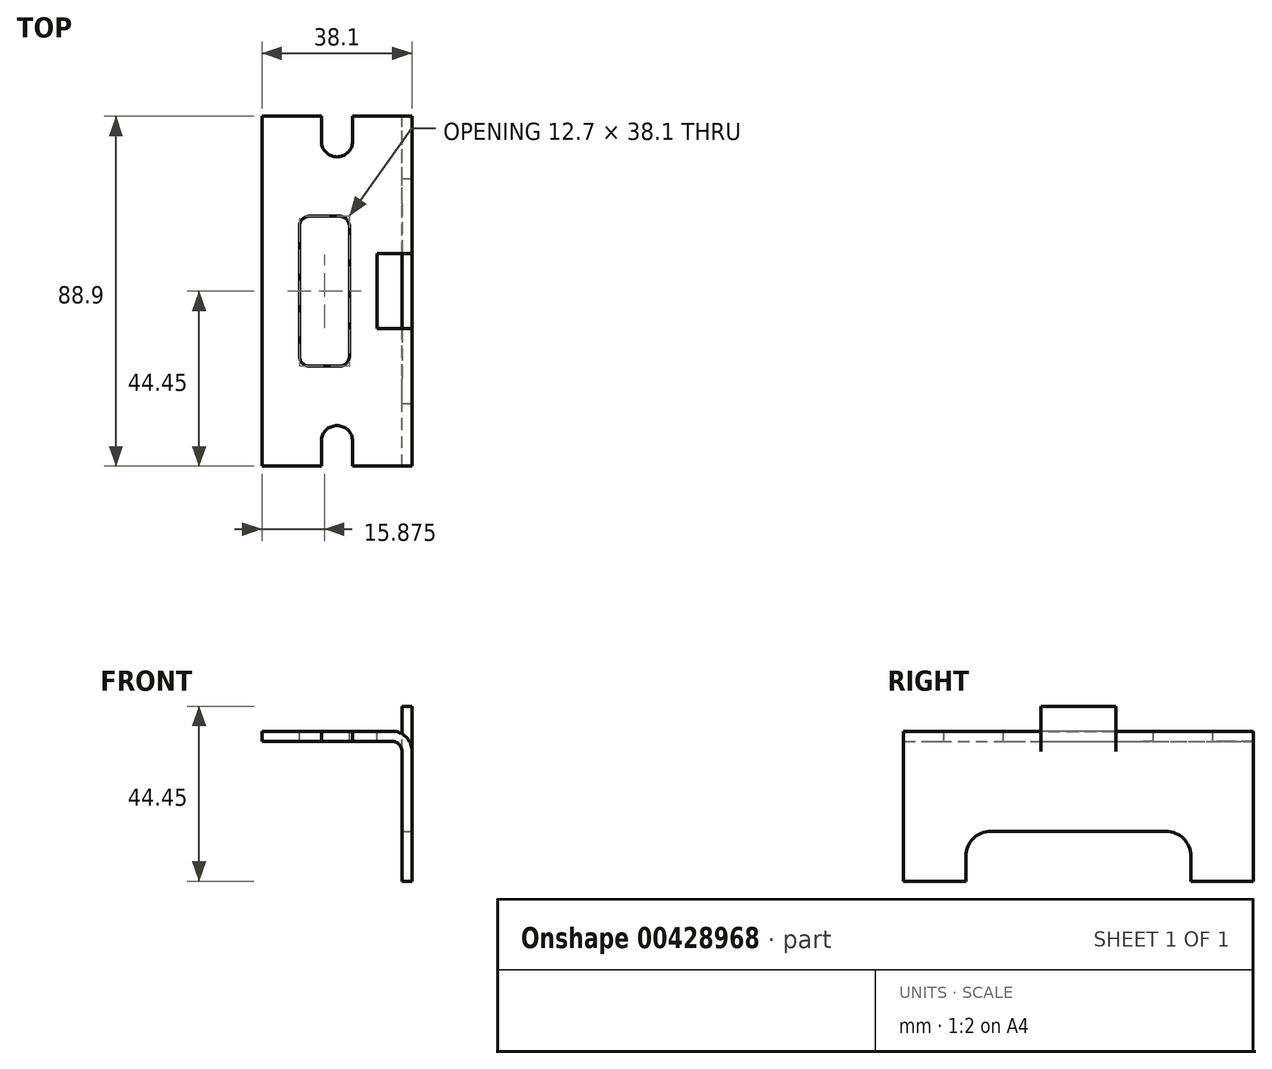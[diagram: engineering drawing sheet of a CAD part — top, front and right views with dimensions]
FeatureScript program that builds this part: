
annotation { "Feature Type Name" : "Feature", "Feature Type Description" : "" }
export const myFeature = defineFeature(function(context is Context, id is Id, definition is map)
    precondition{}
    {
        {
            var Q0;
            Q0=qCreatedBy(makeId("Front.planeOp"),FACE);
            var sketch = newSketch(context, id + "F0", { "sketchPlane" : qUnion([Q0])});
            skLineSegment(sketch, "E0", {"start": v(-5.08, 0) * mm, "end": v(-38.1, 0) * mm});
            skLineSegment(sketch, "E1", {"start": v(0, -38.1) * mm, "end": v(-2.54, -38.1) * mm});
            skLineSegment(sketch, "E2", {"start": v(-2.54, -38.1) * mm, "end": v(-2.54, -5.08) * mm});
            skLineSegment(sketch, "E3", {"start": v(-5.08, -2.54) * mm, "end": v(-38.1, -2.54) * mm});
            skLineSegment(sketch, "E4", {"start": v(-38.1, -2.54) * mm, "end": v(-38.1, 0) * mm});
            skPoint(sketch, "E5.visualSharp", {"position": v(-2.54, -2.54) * mm});
            skArc(sketch, "E5.filletArc", {"start": v(-2.54, -5.08) * mm, "mid": v(-3.28, -3.28) * mm, "end": v(-5.08, -2.54) * mm});
            skLineSegment(sketch, "E6", {"start": v(0, -38.1) * mm, "end": v(0, -3.75) * mm});
            skArc(sketch, "E7.0", {"start": v(0, -5.08) * mm, "mid": v(-1.49, -1.49) * mm, "end": v(-5.08, 0) * mm});
            skPoint(sketch, "E8.orphan", {"position": v(0, 0) * mm});
            skSolve(sketch);
        }
        {
            var Q0;
            Q0 = qSketchRegion(id + "F0", true);
            extrude(context, id + "F1", {"entities" : qUnion([Q0]), "depth" : 88.9 * mm});
        }
        {
            var Q0;
            Q0=makeQuery(id+"F1.opExtrude","SWEPT_FACE",FACE,{"disambiguationData":[OSD([sQuery(id+"F0.wireOp",EDGE,"E0")])]});
            var sketch = newSketch(context, id + "F2", { "sketchPlane" : qUnion([Q0])});
            skLineSegment(sketch, "E9.bottom", {"start": v(-2.54, -34.93) * mm, "end": v(-8.9, -34.93) * mm});
            skLineSegment(sketch, "E9.top", {"start": v(-2.54, -53.98) * mm, "end": v(-8.9, -53.98) * mm});
            skLineSegment(sketch, "E9.left", {"start": v(-2.54, -34.93) * mm, "end": v(-2.54, -53.98) * mm});
            skLineSegment(sketch, "E9.right", {"start": v(-8.9, -34.93) * mm, "end": v(-8.9, -53.98) * mm});
            skPoint(sketch, "E10.bottom.start.orphan", {"position": v(-21.59, -88.9) * mm});
            skPoint(sketch, "E10.top.end.orphan", {"position": v(-5.72, -53.98) * mm});
            skSolve(sketch);
        }
        {
            var Q0;
            Q0=makeQuery(id+"F2.imprint","IMPRINT",FACE,{"disambiguationData":[TD([[makeQuery(id+"F2.imprint","IMPRINT",EDGE,{"derivedFrom":sQuery(id+"F2.wireOp",EDGE,"E9.bottom")}),1.0]])]});
            extrude(context, id + "F3", {"entities" : qUnion([Q0]), "operationType" : NewBodyOperationType.REMOVE, "oppositeDirection" : true, "depth" : 25.4 * mm});
        }
        {
            var Q0;
            Q0=makeQuery(id+"F1.opExtrude","SWEPT_FACE",FACE,{"disambiguationData":[OSD([sQuery(id+"F0.wireOp",EDGE,"E0")])]});
            var sketch = newSketch(context, id + "F4", { "sketchPlane" : qUnion([Q0])});
            skLineSegment(sketch, "E11.bottom", {"start": v(-2.54, -34.93) * mm, "end": v(0, -34.93) * mm});
            skLineSegment(sketch, "E11.top", {"start": v(-2.54, -53.98) * mm, "end": v(0, -53.98) * mm});
            skLineSegment(sketch, "E11.left", {"start": v(-2.54, -34.93) * mm, "end": v(-2.54, -53.98) * mm});
            skLineSegment(sketch, "E11.right", {"start": v(0, -34.93) * mm, "end": v(0, -53.98) * mm});
            skSolve(sketch);
        }
        {
            var Q0;
            Q0 = qSketchRegion(id + "F4", true);
            extrude(context, id + "F5", {"entities" : qUnion([Q0]), "operationType" : NewBodyOperationType.ADD, "depth" : 6.35 * mm, "hasSecondDirection" : true, "secondDirectionOppositeDirection" : true, "secondDirectionDepth" : 6.35 * mm});
        }
        {
            var Q0;
            {var subQ0=sQuery(id+"F2.wireOp",EDGE,"E9.right");Q0=makeQuery(id+"F2.imprint","IMPRINT",FACE,{"disambiguationData":[TD([[makeQuery(id+"F2.imprint","IMPRINT",EDGE,{"derivedFrom":subQ0}),-1.0]])]});}
            var sketch = newSketch(context, id + "F6", { "sketchPlane" : qUnion([Q0])});
            skArc(sketch, "E12", {"start": v(-23.02, -6.35) * mm, "mid": v(-19.05, -10.32) * mm, "end": v(-15.08, -6.35) * mm});
            skArc(sketch, "E13", {"start": v(-15.08, -82.55) * mm, "mid": v(-19.05, -78.58) * mm, "end": v(-23.02, -82.55) * mm});
            skLineSegment(sketch, "E14", {"start": v(-23.02, -6.35) * mm, "end": v(-23.02, 0) * mm});
            skLineSegment(sketch, "E15", {"start": v(-15.08, -6.35) * mm, "end": v(-15.08, 0) * mm});
            skPoint(sketch, "E16.start.orphan", {"position": v(-19.05, 0) * mm});
            skLineSegment(sketch, "E17", {"start": v(-23.02, 0) * mm, "end": v(-15.08, 0) * mm});
            skLineSegment(sketch, "E18", {"start": v(-15.08, -82.55) * mm, "end": v(-15.08, -89) * mm});
            skLineSegment(sketch, "E19", {"start": v(-23.02, -82.55) * mm, "end": v(-23.02, -89) * mm});
            skLineSegment(sketch, "E20", {"start": v(-23.02, -89) * mm, "end": v(-15.08, -89) * mm});
            skSolve(sketch);
        }
        {
            var Q0;
            Q0 = qSketchRegion(id + "F6", true);
            extrude(context, id + "F7", {"entities" : qUnion([Q0]), "operationType" : NewBodyOperationType.REMOVE, "oppositeDirection" : true, "depth" : 25.4 * mm});
        }
        {
            var Q0;
            {var subQ0=sQuery(id+"F2.wireOp",EDGE,"E9.right");Q0=makeQuery(id+"F2.imprint","IMPRINT",FACE,{"disambiguationData":[TD([[makeQuery(id+"F2.imprint","IMPRINT",EDGE,{"derivedFrom":subQ0}),-1.0]])]});}
            var sketch = newSketch(context, id + "F8", { "sketchPlane" : qUnion([Q0])});
            skLineSegment(sketch, "E21.bottom", {"start": v(-26.04, -25.4) * mm, "end": v(-18.42, -25.4) * mm});
            skLineSegment(sketch, "E21.top", {"start": v(-26.03, -63.5) * mm, "end": v(-18.41, -63.5) * mm});
            skLineSegment(sketch, "E21.left", {"start": v(-28.58, -27.94) * mm, "end": v(-28.57, -60.96) * mm});
            skLineSegment(sketch, "E21.right", {"start": v(-15.88, -27.94) * mm, "end": v(-15.87, -60.96) * mm});
            skPoint(sketch, "E22.visualSharp", {"position": v(-28.58, -25.4) * mm});
            skArc(sketch, "E22.filletArc", {"start": v(-26.04, -25.4) * mm, "mid": v(-27.83, -26.14) * mm, "end": v(-28.58, -27.94) * mm});
            skPoint(sketch, "E23.visualSharp", {"position": v(-15.88, -25.4) * mm});
            skArc(sketch, "E23.filletArc", {"start": v(-15.88, -27.94) * mm, "mid": v(-16.62, -26.14) * mm, "end": v(-18.42, -25.4) * mm});
            skPoint(sketch, "E24.visualSharp", {"position": v(-28.57, -63.5) * mm});
            skArc(sketch, "E24.filletArc", {"start": v(-28.57, -60.96) * mm, "mid": v(-27.83, -62.76) * mm, "end": v(-26.03, -63.5) * mm});
            skPoint(sketch, "E25.visualSharp", {"position": v(-15.87, -63.5) * mm});
            skArc(sketch, "E25.filletArc", {"start": v(-18.41, -63.5) * mm, "mid": v(-16.62, -62.76) * mm, "end": v(-15.88, -60.96) * mm});
            skSolve(sketch);
        }
        {
            var Q0;
            Q0 = qSketchRegion(id + "F8", true);
            extrude(context, id + "F9", {"entities" : qUnion([Q0]), "operationType" : NewBodyOperationType.REMOVE, "oppositeDirection" : true, "depth" : 25.4 * mm});
        }
        {
            var Q0;
            Q0=makeQuery(id+"F5.boolean.opBoolean","MERGE",FACE,{"derivedFrom":[makeQuery(id+"F1.opExtrude","SWEPT_FACE",FACE,{"disambiguationData":[OSD([sQuery(id+"F0.wireOp",EDGE,"E6")])]}),makeQuery(id+"F5.opExtrude","SWEPT_FACE",FACE,{"disambiguationData":[OSD([sQuery(id+"F4.wireOp",EDGE,"E11.right")])]})]});
            var sketch = newSketch(context, id + "F10", { "sketchPlane" : qUnion([Q0])});
            skLineSegment(sketch, "E26.bottom", {"start": v(-73.03, -38.1) * mm, "end": v(-15.88, -38.1) * mm});
            skLineSegment(sketch, "E26.top", {"start": v(-66.68, -25.4) * mm, "end": v(-22.23, -25.4) * mm});
            skLineSegment(sketch, "E26.left", {"start": v(-73.03, -38.1) * mm, "end": v(-73.03, -31.75) * mm});
            skLineSegment(sketch, "E26.right", {"start": v(-15.88, -38.1) * mm, "end": v(-15.88, -31.75) * mm});
            skPoint(sketch, "E27.visualSharp", {"position": v(-73.03, -25.4) * mm});
            skArc(sketch, "E27.filletArc", {"start": v(-66.68, -25.4) * mm, "mid": v(-71.17, -27.26) * mm, "end": v(-73.03, -31.75) * mm});
            skPoint(sketch, "E28.visualSharp", {"position": v(-15.88, -25.4) * mm});
            skArc(sketch, "E28.filletArc", {"start": v(-15.87, -31.75) * mm, "mid": v(-17.73, -27.26) * mm, "end": v(-22.23, -25.4) * mm});
            skSolve(sketch);
        }
        {
            var Q0;
            Q0 = qSketchRegion(id + "F10", true);
            extrude(context, id + "F11", {"entities" : qUnion([Q0]), "operationType" : NewBodyOperationType.REMOVE, "oppositeDirection" : true, "depth" : 25.4 * mm});
        }
    });
